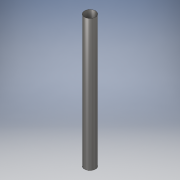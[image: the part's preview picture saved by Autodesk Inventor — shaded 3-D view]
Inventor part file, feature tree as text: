
AUTODESK INVENTOR PART (.ipt)
format: ipt  version: 2018 (Build 220112000, 112)  size: 95,744 bytes
history: native  units: in
note: dims shown in document units (in); Inventor stores cm internally (conversion verified against a paired STEP export)
features: extrude x1, sketch x1
ambient origin geometry x8: Origin, YZ Plane, XZ Plane, XY Plane, X Axis, Y Axis, Z Axis, Center Point
bodies: Solid1 (feature_tree)
feature tree (2):
  extrude  "Extrusion1"  Depth=24.0in
  sketch  "Sketch1"  dims[d0=2.0in d1=1.99in d2=24.0in d3=0.0in]
